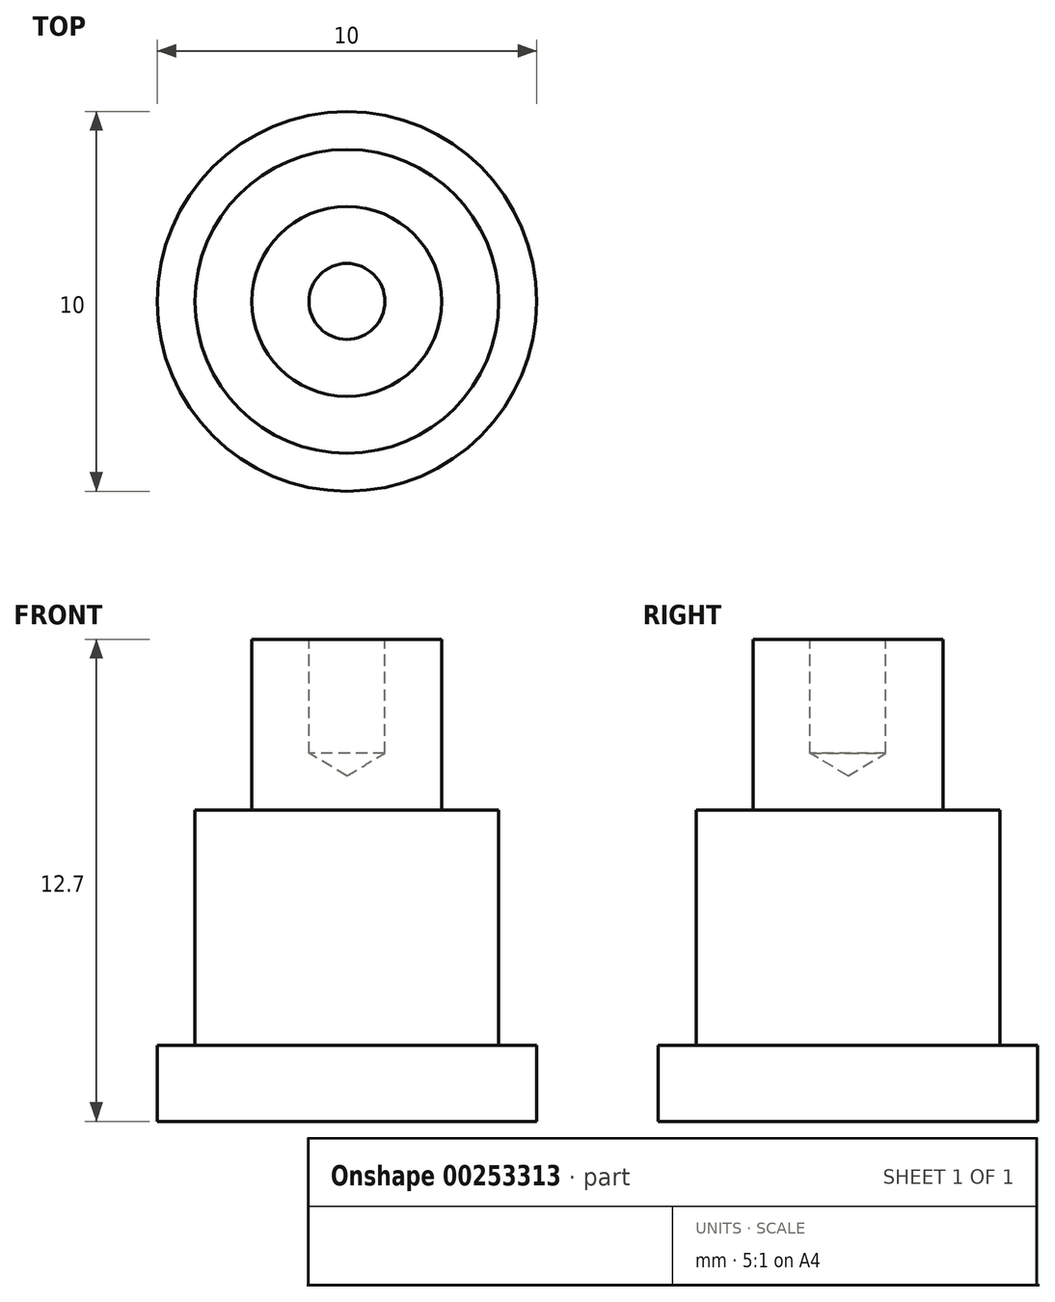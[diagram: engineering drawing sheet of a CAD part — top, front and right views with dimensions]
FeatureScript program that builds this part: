
annotation { "Feature Type Name" : "Feature", "Feature Type Description" : "" }
export const myFeature = defineFeature(function(context is Context, id is Id, definition is map)
    precondition{}
    {
        {
            var Q0;
            Q0=qCreatedBy(makeId("Top.planeOp"),FACE);
            var sketch = newSketch(context, id + "F0", { "sketchPlane" : qUnion([Q0])});
            skCircle(sketch, "E0", {"center": v(0, 0) * mm, "radius": 5 * mm});
            skCircle(sketch, "E1", {"center": v(0, 0) * mm, "radius": 4 * mm});
            skCircle(sketch, "E2", {"center": v(0, 0) * mm, "radius": 2.5 * mm});
            skSolve(sketch);
        }
        {
            var Q0;
            Q0=makeQuery(id+"F0.imprint","IMPRINT",FACE,{"disambiguationData":[TD([[makeQuery(id+"F0.imprint","IMPRINT",EDGE,{"derivedFrom":sQuery(id+"F0.wireOp",EDGE,"E2")}),1.0]])]});
            extrude(context, id + "F1", {"entities" : qUnion([Q0]), "depth" : (4.5 + 6.2 + 2) * mm});
        }
        {
            var Q0;
            Q0=makeQuery(id+"F0.imprint","IMPRINT",FACE,{"disambiguationData":[TD([[makeQuery(id+"F0.imprint","IMPRINT",EDGE,{"derivedFrom":sQuery(id+"F0.wireOp",EDGE,"E1")}),1.0]])]});
            extrude(context, id + "F2", {"entities" : qUnion([Q0]), "operationType" : NewBodyOperationType.ADD, "depth" : 8.2 * mm});
        }
        {
            var Q0;
            Q0=makeQuery(id+"F0.imprint","IMPRINT",FACE,{"disambiguationData":[TD([[makeQuery(id+"F0.imprint","IMPRINT",EDGE,{"derivedFrom":sQuery(id+"F0.wireOp",EDGE,"E0")}),1.0]])]});
            extrude(context, id + "F3", {"entities" : qUnion([Q0]), "operationType" : NewBodyOperationType.ADD, "depth" : 2 * mm});
        }
        {
            var Q0;
            Q0=makeQuery(id+"F1.opExtrude","CAP_FACE",FACE,{"disambiguationData":[OSD([sQuery(id+"F0.wireOp",EDGE,"E2")])],"isStart":false});
            var sketch = newSketch(context, id + "F4", { "sketchPlane" : qUnion([Q0])});
            skPoint(sketch, "E3", {"position": v(0, 0) * mm});
            skSolve(sketch);
        }
        {
            var Q0;
            Q0=sQuery(id+"F4.wireOp",VERTEX,"E3");
            var Q1;
            Q1=makeQuery(id+"F1.opExtrude","SWEPT_BODY",BODY,{"disambiguationData":[OSD([sQuery(id+"F0.wireOp",EDGE,"E2")])]});
            hole(context, id + "F5", {"style" : HoleStyle.SIMPLE, "endStyle" : HoleEndStyle.BLIND, "holeDiameter" : 2 * mm, "holeDepth" : 3 * mm, "tappedDepth" : 12 * mm, "tapClearance" : 3, "locations" : qUnion([Q0]), "scope" : qUnion([Q1])});
        }
    });
